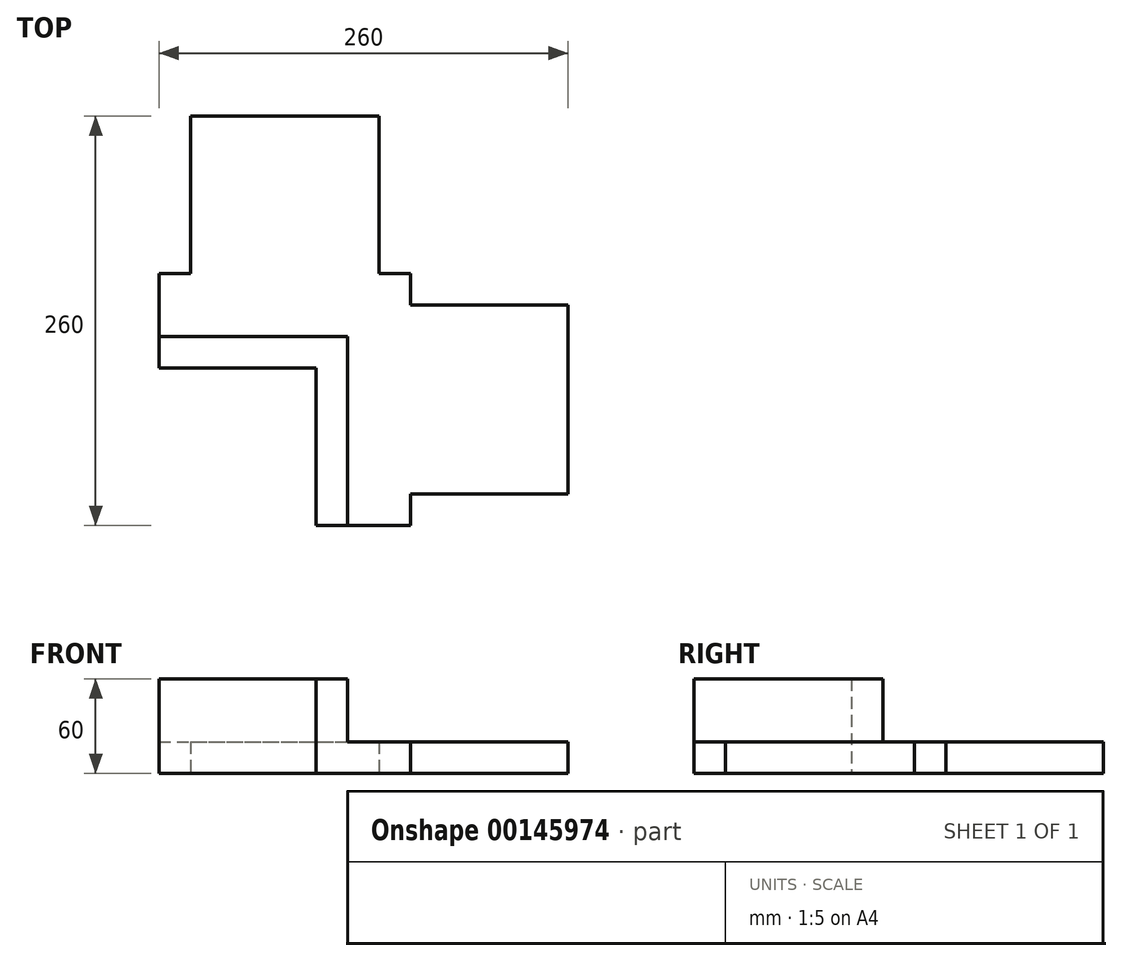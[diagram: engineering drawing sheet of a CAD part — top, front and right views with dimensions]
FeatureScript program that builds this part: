
annotation { "Feature Type Name" : "Feature", "Feature Type Description" : "" }
export const myFeature = defineFeature(function(context is Context, id is Id, definition is map)
    precondition{}
    {
        {
            var Q0;
            Q0=qCreatedBy(makeId("Top.planeOp"),FACE);
            var sketch = newSketch(context, id + "F0", { "sketchPlane" : qUnion([Q0])});
            skLineSegment(sketch, "E0", {"start": v(-38.38, 0) * mm, "end": v(61.62, 0) * mm});
            skLineSegment(sketch, "E1", {"start": v(-38.38, 0) * mm, "end": v(-38.38, 60) * mm});
            skLineSegment(sketch, "E2", {"start": v(-38.38, 60) * mm, "end": v(-18.38, 60) * mm});
            skLineSegment(sketch, "E3", {"start": v(-18.38, 60) * mm, "end": v(-18.38, 160) * mm});
            skLineSegment(sketch, "E4", {"start": v(-18.38, 160) * mm, "end": v(101.62, 160) * mm});
            skLineSegment(sketch, "E5", {"start": v(101.62, 160) * mm, "end": v(101.62, 60) * mm});
            skLineSegment(sketch, "E6", {"start": v(101.62, 60) * mm, "end": v(121.62, 60) * mm});
            skLineSegment(sketch, "E7", {"start": v(121.62, 60) * mm, "end": v(61.62, 0) * mm});
            skLineSegment(sketch, "E8.MirrorCS", {"start": v(61.62, -100) * mm, "end": v(61.62, 0) * mm});
            skLineSegment(sketch, "E9.MirrorCS", {"start": v(61.62, -100) * mm, "end": v(121.62, -100) * mm});
            skLineSegment(sketch, "E10.MirrorCS", {"start": v(121.62, -100) * mm, "end": v(121.62, -80) * mm});
            skLineSegment(sketch, "E11.MirrorCS", {"start": v(121.62, -80) * mm, "end": v(221.62, -80) * mm});
            skLineSegment(sketch, "E12.MirrorCS", {"start": v(221.62, -80) * mm, "end": v(221.62, 40) * mm});
            skLineSegment(sketch, "E13.MirrorCS", {"start": v(221.62, 40) * mm, "end": v(121.62, 40) * mm});
            skLineSegment(sketch, "E14.MirrorCS", {"start": v(121.62, 40) * mm, "end": v(121.62, 60) * mm});
            skSolve(sketch);
        }
        {
            var Q0;
            Q0 = qSketchRegion(id + "F0", true);
            extrude(context, id + "F1", {"entities" : qUnion([Q0]), "depth" : 20 * mm});
        }
        {
            var Q0;
            Q0=makeQuery(id+"F1.opExtrude","CAP_FACE",FACE,{"disambiguationData":[OSD([sQuery(id+"F0.wireOp",EDGE,"E0"),sQuery(id+"F0.wireOp",EDGE,"E1"),sQuery(id+"F0.wireOp",EDGE,"E2"),sQuery(id+"F0.wireOp",EDGE,"E3"),sQuery(id+"F0.wireOp",EDGE,"E4"),sQuery(id+"F0.wireOp",EDGE,"E5"),sQuery(id+"F0.wireOp",EDGE,"E6"),sQuery(id+"F0.wireOp",EDGE,"E8.MirrorCS"),sQuery(id+"F0.wireOp",EDGE,"E9.MirrorCS"),sQuery(id+"F0.wireOp",EDGE,"E10.MirrorCS"),sQuery(id+"F0.wireOp",EDGE,"E11.MirrorCS"),sQuery(id+"F0.wireOp",EDGE,"E12.MirrorCS"),sQuery(id+"F0.wireOp",EDGE,"E13.MirrorCS"),sQuery(id+"F0.wireOp",EDGE,"E14.MirrorCS")])],"isStart":false});
            var sketch = newSketch(context, id + "F2", { "sketchPlane" : qUnion([Q0])});
            skLineSegment(sketch, "E15.bottom", {"start": v(-38.38, 0) * mm, "end": v(61.62, 0) * mm});
            skLineSegment(sketch, "E15.top", {"start": v(-38.38, 20) * mm, "end": v(81.62, 20) * mm});
            skLineSegment(sketch, "E15.left", {"start": v(-38.38, 0) * mm, "end": v(-38.38, 20) * mm});
            skLineSegment(sketch, "E15.right", {"start": v(81.62, 0) * mm, "end": v(81.62, 20) * mm});
            skLineSegment(sketch, "E16.bottom", {"start": v(61.62, -100) * mm, "end": v(81.62, -100) * mm});
            skLineSegment(sketch, "E16.left", {"start": v(61.62, -100) * mm, "end": v(61.62, 0) * mm});
            skLineSegment(sketch, "E16.right", {"start": v(81.62, -100) * mm, "end": v(81.62, 0) * mm});
            skSolve(sketch);
        }
        {
            var Q0;
            Q0 = qSketchRegion(id + "F2", true);
            extrude(context, id + "F3", {"entities" : qUnion([Q0]), "operationType" : NewBodyOperationType.ADD, "depth" : 40 * mm});
        }
    });
